# Revit family: prv-c-small
name_source: partatom
category: Generic Models
revit_build: Autodesk Revit 2015 (Build: 20140322_1515(x64)
units: mm (PartAtom-declared; Revit-internal decimal feet)

## types (3) — shared parameters
Body and Cage = Bronze
Pressure Adjusting screw = Stainless Steel, Polished
h = 1.3 "

## per-type parameters (varying)
| type | 2hex L | 2hex thk | DU-IPS-C | DU-IPS-C' | H | HEX | Rev1 | Rev2 | Size | Size Radius | ext1 | ext2 | hex rp | hex thk |
| PRV0.50-SU-IPS-C | 0.38 " | 0.15 " | 3.8 " | 2.34 " | 3.94 " | 1.55 " | 1.55 " | 0.12 " | 0.5 " | 0.25 " | 0.6 " | 0.4 " | 1.5 " | 0.53 " |
| PRV0.75-SU-IPS-C | 0.42 " | 0.17 " | 4.06 " | 2.5 " | 3.94 " | 1.55 " | 1.65 " | 0.13 " | 0.75 " | 0.38 " | 0.7 " | 0.4 " | 1.6 " | 0.55 " |
| PRV1.00-SU-IPS-C | 0.75 " | 0.25 " | 6.28 " | 3.86 " | 4.96 " | 2.25 " | 1.75 " | 0.2 " | 1 " | 0.5 " | 0.8 " | 1 " | 2.75 " | 0.75 " |

## geometry (parser evidence)
native form markers: Sweep x2
no freeform markers — native parametric forms only
